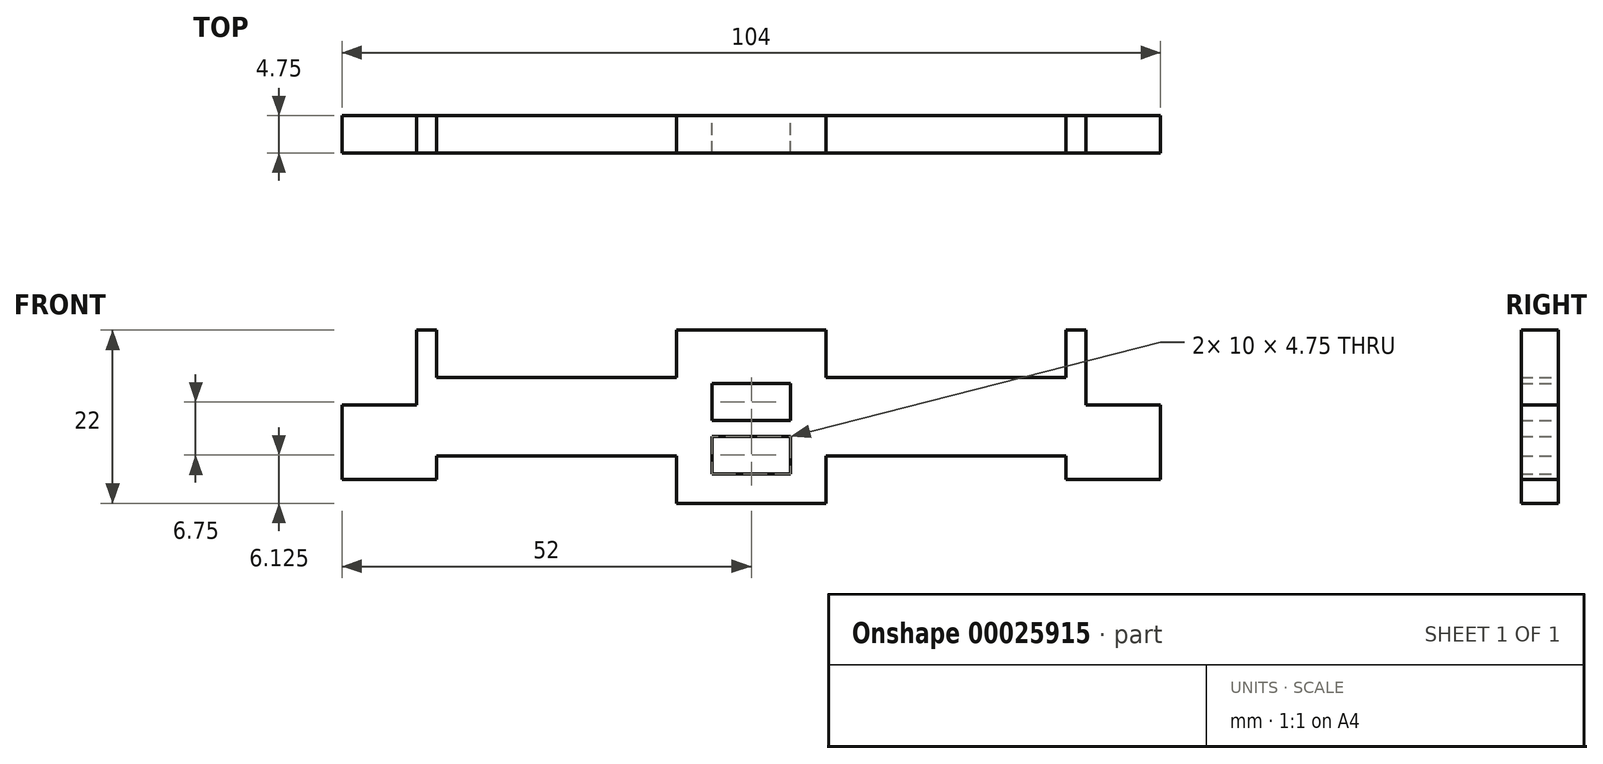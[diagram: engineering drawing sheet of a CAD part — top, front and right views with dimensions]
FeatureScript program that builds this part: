
annotation { "Feature Type Name" : "Feature", "Feature Type Description" : "" }
export const myFeature = defineFeature(function(context is Context, id is Id, definition is map)
    precondition{}
    {
        {
            var Q0;
            Q0=qCreatedBy(makeId("Front.planeOp"),FACE);
            var sketch = newSketch(context, id + "F0", { "sketchPlane" : qUnion([Q0])});
            skLineSegment(sketch, "E0", {"start": v(0, -6) * mm, "end": v(9.5, -6) * mm});
            skLineSegment(sketch, "E1", {"start": v(9.5, -6) * mm, "end": v(9.5, 0) * mm});
            skLineSegment(sketch, "E2", {"start": v(9.5, 0) * mm, "end": v(40, 0) * mm});
            skLineSegment(sketch, "E3", {"start": v(40, 0) * mm, "end": v(40, -3) * mm});
            skLineSegment(sketch, "E4", {"start": v(40, -3) * mm, "end": v(52, -3) * mm});
            skLineSegment(sketch, "E5", {"start": v(52, -3) * mm, "end": v(52, 6.5) * mm});
            skLineSegment(sketch, "E6", {"start": v(52, 6.5) * mm, "end": v(42.5, 6.5) * mm});
            skLineSegment(sketch, "E7", {"start": v(42.5, 6.5) * mm, "end": v(42.5, 16) * mm});
            skLineSegment(sketch, "E8", {"start": v(42.5, 16) * mm, "end": v(40, 16) * mm});
            skLineSegment(sketch, "E9", {"start": v(40, 16) * mm, "end": v(40, 10) * mm});
            skLineSegment(sketch, "E10", {"start": v(40, 10) * mm, "end": v(9.5, 10) * mm});
            skLineSegment(sketch, "E11", {"start": v(9.5, 10) * mm, "end": v(9.5, 16) * mm});
            skLineSegment(sketch, "E12", {"start": v(9.5, 16) * mm, "end": v(0, 16) * mm});
            skLineSegment(sketch, "E13", {"start": v(0, 16) * mm, "end": v(0, 9.25) * mm});
            skLineSegment(sketch, "E14.bottom", {"start": v(0, 9.25) * mm, "end": v(5, 9.25) * mm});
            skLineSegment(sketch, "E14.top", {"start": v(0, 4.5) * mm, "end": v(5, 4.5) * mm});
            skLineSegment(sketch, "E14.right", {"start": v(5, 9.25) * mm, "end": v(5, 4.5) * mm});
            skLineSegment(sketch, "E15.bottom", {"start": v(0, 2.5) * mm, "end": v(5, 2.5) * mm});
            skLineSegment(sketch, "E15.top", {"start": v(0, -2.25) * mm, "end": v(5, -2.25) * mm});
            skLineSegment(sketch, "E15.right", {"start": v(5, 2.5) * mm, "end": v(5, -2.25) * mm});
            skLineSegment(sketch, "E16.trimOffspring", {"start": v(0, -2.25) * mm, "end": v(0, -6) * mm});
            skLineSegment(sketch, "E17.trimOffspring", {"start": v(0, 4.5) * mm, "end": v(0, 2.5) * mm});
            skSolve(sketch);
        }
        {
            var Q0;
            Q0=makeQuery(id+"F0.imprint","IMPRINT",FACE,{"disambiguationData":[TD([[makeQuery(id+"F0.imprint","IMPRINT",EDGE,{"derivedFrom":sQuery(id+"F0.wireOp",EDGE,"E0")}),1.0]])]});
            extrude(context, id + "F1", {"entities" : qUnion([Q0]), "depth" : 4.75 * mm});
        }
        {
            var Q0;
            Q0=makeQuery(id+"F1.opExtrude","SWEPT_BODY",BODY,{"disambiguationData":[OSD([sQuery(id+"F0.wireOp",EDGE,"E0"),sQuery(id+"F0.wireOp",EDGE,"E1"),sQuery(id+"F0.wireOp",EDGE,"E2"),sQuery(id+"F0.wireOp",EDGE,"E3"),sQuery(id+"F0.wireOp",EDGE,"E4"),sQuery(id+"F0.wireOp",EDGE,"E5"),sQuery(id+"F0.wireOp",EDGE,"E6"),sQuery(id+"F0.wireOp",EDGE,"E7"),sQuery(id+"F0.wireOp",EDGE,"E8"),sQuery(id+"F0.wireOp",EDGE,"E9"),sQuery(id+"F0.wireOp",EDGE,"E10"),sQuery(id+"F0.wireOp",EDGE,"E11"),sQuery(id+"F0.wireOp",EDGE,"E12"),sQuery(id+"F0.wireOp",EDGE,"E13")])]});
            var Q1;
            Q1=qCreatedBy(makeId("Right.planeOp"),FACE);
            mirror(context, id + "F2", {"operationType" : NewBodyOperationType.ADD, "entities" : qUnion([Q0]), "mirrorPlane" : qUnion([Q1])});
        }
    });
